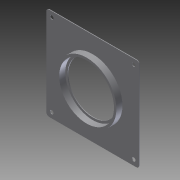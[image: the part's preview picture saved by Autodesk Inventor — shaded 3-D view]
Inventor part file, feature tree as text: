
AUTODESK INVENTOR PART (.ipt)
format: ipt  version: 2011 (Build 150239000, 239)  size: 125,952 bytes
history: native  units: in
note: dims shown in document units (in); Inventor stores cm internally (conversion verified against a paired STEP export)
features: extrude x5, sketch x5, fillet x1
ambient origin geometry x8: Origin, YZ Plane, XZ Plane, XY Plane, X Axis, Y Axis, Z Axis, Center Point
bodies: Solid1 (feature_tree)
feature tree (11):
  extrude  "Extrusion1"  Depth=4.0in
  extrude  "Extrusion2"  Depth=2.16in
  extrude  "Extrusion3"  Depth=1.7655in
  extrude  "Extrusion4"  Depth=0.029in TaperAngle=0.0deg
  extrude  "Extrusion5"  Depth=2.36in
  fillet  "Fillet1"  Radius=2.56in
  sketch  "Sketch1"  dims[d0=4.0in d1=4.0in]
  sketch  "Sketch2"  dims[d2=0.029in d3=0.0in d4=2.16in]
  sketch  "Sketch3"  dims[d5=0.029in d6=0.0in d7=1.7655in]
  sketch  "Sketch4"  dims[d8=0.156in d9=0.029in d10=0.0in]
  sketch  "Sketch5"  dims[d11=0.029in d12=0.0in d13=2.36in d14=2.56in d15=0.262in d16=0.0in d17=0.125in]
